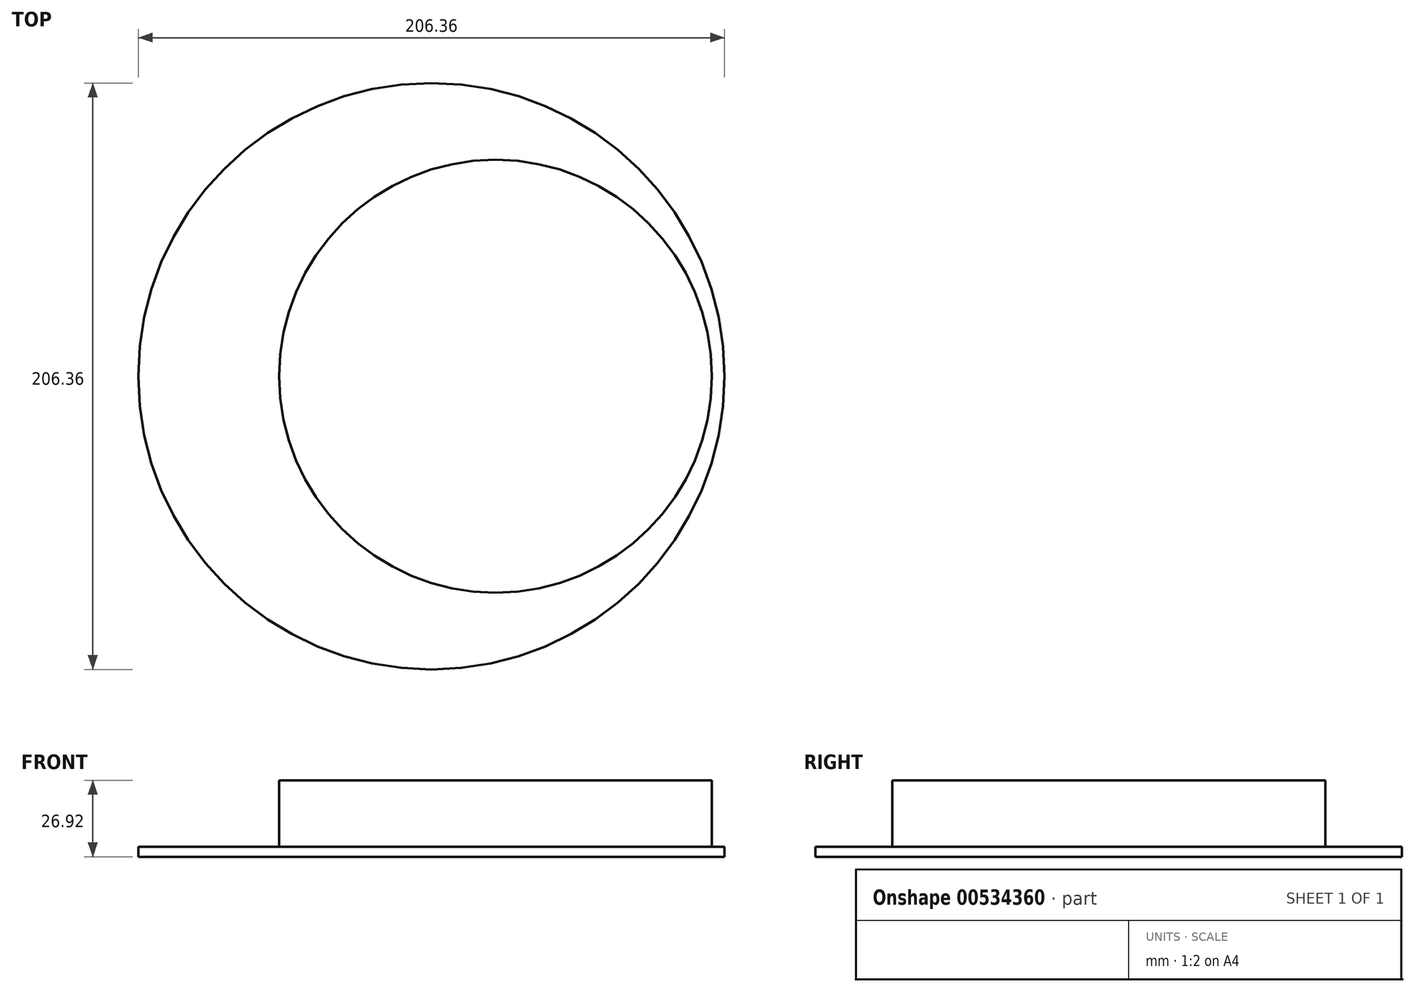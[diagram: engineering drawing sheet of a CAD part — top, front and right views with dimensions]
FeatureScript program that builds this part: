
annotation { "Feature Type Name" : "Feature", "Feature Type Description" : "" }
export const myFeature = defineFeature(function(context is Context, id is Id, definition is map)
    precondition{}
    {
        {
            var Q0;
            Q0=qCreatedBy(makeId("Top.planeOp"),FACE);
            var sketch = newSketch(context, id + "F0", { "sketchPlane" : qUnion([Q0])});
            skCircle(sketch, "E0", {"center": v(0, 0) * mm, "radius": 76.16 * mm});
            skSolve(sketch);
        }
        {
            var Q0;
            Q0 = qSketchRegion(id + "F0", true);
            extrude(context, id + "F1", {"entities" : qUnion([Q0]), "depth" : 26.92 * mm, "offsetDistance" : 25.4 * mm});
        }
        {
            var Q0;
            Q0=qCreatedBy(makeId("Top.planeOp"),FACE);
            var sketch = newSketch(context, id + "F2", { "sketchPlane" : qUnion([Q0])});
            skCircle(sketch, "E1", {"center": v(-22.53, 0) * mm, "radius": 103.18 * mm});
            skSolve(sketch);
        }
        {
            var Q0;
            Q0 = qSketchRegion(id + "F2", true);
            extrude(context, id + "F3", {"entities" : qUnion([Q0]), "operationType" : NewBodyOperationType.ADD, "depth" : 25.4 * mm, "offsetDistance" : 25.4 * mm});
        }
        {
            var Q0;
            Q0=makeQuery(id+"F3.opExtrude","CAP_FACE",FACE,{"disambiguationData":[OSD([sQuery(id+"F2.wireOp",EDGE,"E1")])],"isStart":false});
            extrude(context, id + "F4", {"entities" : qUnion([Q0]), "operationType" : NewBodyOperationType.REMOVE, "oppositeDirection" : true, "depth" : 21.84 * mm, "offsetDistance" : 25.4 * mm});
        }
    });
